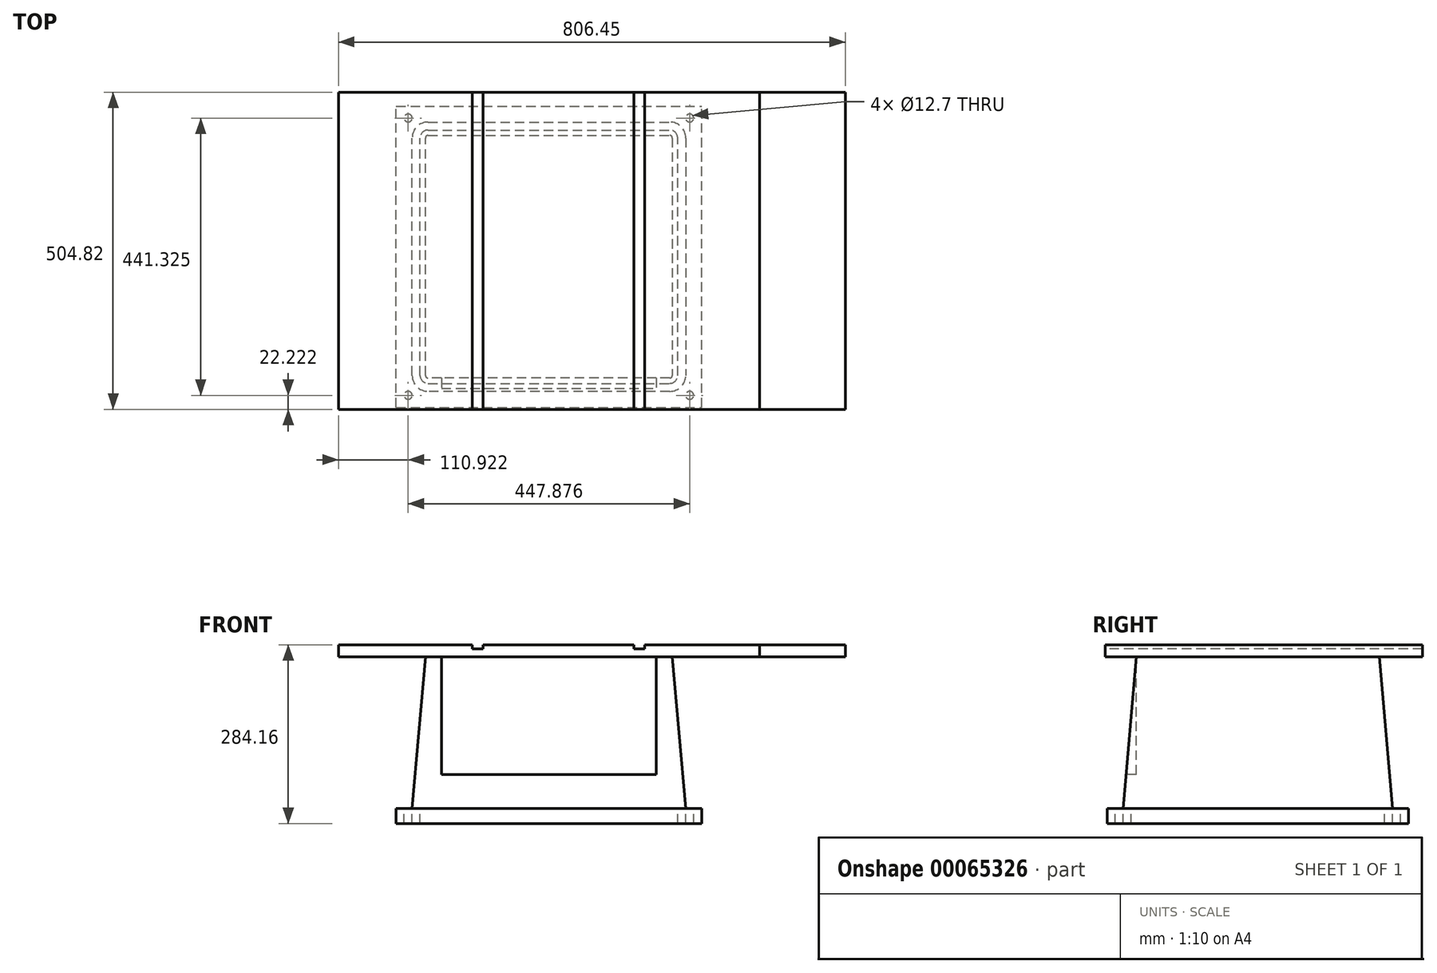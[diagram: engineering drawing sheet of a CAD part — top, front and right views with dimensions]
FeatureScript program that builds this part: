
annotation { "Feature Type Name" : "Feature", "Feature Type Description" : "" }
export const myFeature = defineFeature(function(context is Context, id is Id, definition is map)
    precondition{}
    {
        {
            var Q0;
            Q0=qCreatedBy(makeId("Top.planeOp"),FACE);
            var sketch = newSketch(context, id + "F0", { "sketchPlane" : qUnion([Q0])});
            skLineSegment(sketch, "E0.bottom", {"start": v(334.96, 252.41) * mm, "end": v(-334.96, 252.41) * mm});
            skLineSegment(sketch, "E0.top", {"start": v(334.96, -252.41) * mm, "end": v(-334.96, -252.41) * mm});
            skLineSegment(sketch, "E0.left", {"start": v(334.96, 252.41) * mm, "end": v(334.96, -252.41) * mm});
            skLineSegment(sketch, "E0.right", {"start": v(-334.96, 252.41) * mm, "end": v(-334.96, -252.41) * mm});
            skPoint(sketch, "E0.middle", {"position": v(0, 0) * mm});
            skSolve(sketch);
        }
        {
            var Q0;
            Q0=makeQuery(id+"F0.imprint","IMPRINT",FACE,{"disambiguationData":[TD([[makeQuery(id+"F0.imprint","IMPRINT",EDGE,{"derivedFrom":sQuery(id+"F0.wireOp",EDGE,"E0.bottom")}),1.0]])]});
            extrude(context, id + "F1", {"entities" : qUnion([Q0]), "oppositeDirection" : true, "depth" : 19.05 * mm, "offsetDistance" : 25.4 * mm});
        }
        {
            var Q0;
            Q0=makeQuery(id+"F1.opExtrude","SWEPT_FACE",FACE,{"disambiguationData":[OSD([sQuery(id+"F0.wireOp",EDGE,"E0.left")])]});
            extrude(context, id + "F2", {"entities" : qUnion([Q0]), "depth" : 136.53 * mm, "offsetDistance" : 25.4 * mm});
        }
        {
            var Q0;
            Q0=makeQuery(id+"F0.imprint","IMPRINT",FACE,{"disambiguationData":[TD([[makeQuery(id+"F0.imprint","IMPRINT",EDGE,{"derivedFrom":sQuery(id+"F0.wireOp",EDGE,"E0.bottom")}),1.0]])]});
            cPlane(context, id + "F3", {"entities" : qUnion([Q0]), "cplaneType" : CPlaneType.OFFSET, "offset" : 260.35 * mm, "oppositeDirection" : true, "width" : 152.4 * mm, "height" : 152.4 * mm});
        }
        {
            var Q0;
            Q0=qCreatedBy(id+"F3.planeOp",FACE);
            var sketch = newSketch(context, id + "F4", { "sketchPlane" : qUnion([Q0])});
            skLineSegment(sketch, "E1.bottom", {"start": v(-243.09, -249.24) * mm, "end": v(242.89, -249.24) * mm});
            skLineSegment(sketch, "E1.top", {"start": v(-243.09, 230.19) * mm, "end": v(242.89, 230.19) * mm});
            skLineSegment(sketch, "E1.left", {"start": v(-243.09, -249.24) * mm, "end": v(-243.09, 230.19) * mm});
            skLineSegment(sketch, "E1.right", {"start": v(242.89, -249.24) * mm, "end": v(242.89, 230.19) * mm});
            skLineSegment(sketch, "E2.bottom", {"start": v(-224.04, 211.14) * mm, "end": v(223.84, 211.14) * mm, "construction": true});
            skLineSegment(sketch, "E2.top", {"start": v(-224.04, -230.19) * mm, "end": v(223.84, -230.19) * mm, "construction": true});
            skLineSegment(sketch, "E2.left", {"start": v(-224.04, 211.14) * mm, "end": v(-224.04, -230.19) * mm, "construction": true});
            skLineSegment(sketch, "E2.right", {"start": v(223.84, 211.14) * mm, "end": v(223.84, -230.19) * mm, "construction": true});
            skCircle(sketch, "E3", {"center": v(-224.04, 211.14) * mm, "radius": 6.35 * mm});
            skCircle(sketch, "E4", {"center": v(-224.04, -230.19) * mm, "radius": 6.35 * mm});
            skCircle(sketch, "E5", {"center": v(223.84, -230.19) * mm, "radius": 6.35 * mm});
            skCircle(sketch, "E6", {"center": v(223.84, 211.14) * mm, "radius": 6.35 * mm});
            skLineSegment(sketch, "E7.bottom", {"start": v(-192.29, -223.84) * mm, "end": v(192.09, -223.84) * mm});
            skLineSegment(sketch, "E7.top", {"start": v(-192.29, 204.79) * mm, "end": v(192.09, 204.79) * mm});
            skLineSegment(sketch, "E7.left", {"start": v(-217.69, -198.44) * mm, "end": v(-217.69, 179.39) * mm});
            skLineSegment(sketch, "E7.right", {"start": v(217.49, -198.44) * mm, "end": v(217.49, 179.39) * mm});
            skPoint(sketch, "E8.visualSharp", {"position": v(217.49, 204.79) * mm});
            skArc(sketch, "E8.filletArc", {"start": v(217.49, 179.39) * mm, "mid": v(210.05, 197.35) * mm, "end": v(192.09, 204.79) * mm});
            skPoint(sketch, "E9.visualSharp", {"position": v(-217.69, 204.79) * mm});
            skArc(sketch, "E9.filletArc", {"start": v(-192.29, 204.79) * mm, "mid": v(-210.25, 197.35) * mm, "end": v(-217.69, 179.39) * mm});
            skPoint(sketch, "E10.visualSharp", {"position": v(-217.69, -223.84) * mm});
            skArc(sketch, "E10.filletArc", {"start": v(-217.69, -198.44) * mm, "mid": v(-210.25, -216.4) * mm, "end": v(-192.29, -223.84) * mm});
            skPoint(sketch, "E11.visualSharp", {"position": v(217.49, -223.84) * mm});
            skArc(sketch, "E11.filletArc", {"start": v(192.09, -223.84) * mm, "mid": v(210.05, -216.4) * mm, "end": v(217.49, -198.44) * mm});
            skSolve(sketch);
        }
        {
            var Q0;
            Q0=makeQuery(id+"F4.imprint","IMPRINT",FACE,{"disambiguationData":[TD([[makeQuery(id+"F4.imprint","IMPRINT",EDGE,{"derivedFrom":sQuery(id+"F4.wireOp",EDGE,"E7.bottom")}),1.0]])]});
            extrude(context, id + "F5", {"entities" : qUnion([Q0]), "operationType" : NewBodyOperationType.ADD, "endBound" : BoundingType.UP_TO_NEXT, "depth" : 25.4 * mm, "offsetDistance" : 25.4 * mm, "hasDraft" : true, "draftAngle" : 5 * degree, "draftPullDirection" : true});
        }
        {
            var Q0;
            Q0=makeQuery(id+"F5.opExtrude","CAP_FACE",FACE,{"disambiguationData":[OSD([sQuery(id+"F4.wireOp",EDGE,"E7.bottom"),sQuery(id+"F4.wireOp",EDGE,"E7.top"),sQuery(id+"F4.wireOp",EDGE,"E7.left"),sQuery(id+"F4.wireOp",EDGE,"E7.right"),sQuery(id+"F4.wireOp",EDGE,"E8.filletArc"),sQuery(id+"F4.wireOp",EDGE,"E9.filletArc"),sQuery(id+"F4.wireOp",EDGE,"E10.filletArc"),sQuery(id+"F4.wireOp",EDGE,"E11.filletArc")])],"isStart":true});
            var sketch = newSketch(context, id + "F6", { "sketchPlane" : qUnion([Q0])});
            skLineSegment(sketch, "E12.0", {"start": v(-192.29, 223.84) * mm, "end": v(192.09, 223.84) * mm});
            skLineSegment(sketch, "E13.0.0", {"start": v(-192.29, -204.79) * mm, "end": v(192.09, -204.79) * mm});
            skArc(sketch, "E13.0.1", {"start": v(192.09, -204.79) * mm, "mid": v(210.05, -197.35) * mm, "end": v(217.49, -179.39) * mm});
            skLineSegment(sketch, "E13.0.2", {"start": v(217.49, 198.44) * mm, "end": v(217.49, -179.39) * mm});
            skArc(sketch, "E13.0.3", {"start": v(217.49, 198.44) * mm, "mid": v(210.05, 216.4) * mm, "end": v(192.09, 223.84) * mm});
            skArc(sketch, "E13.0.5", {"start": v(-192.29, 223.84) * mm, "mid": v(-210.25, 216.4) * mm, "end": v(-217.69, 198.44) * mm});
            skLineSegment(sketch, "E13.0.6", {"start": v(-217.69, 198.44) * mm, "end": v(-217.69, -179.39) * mm});
            skArc(sketch, "E13.0.7", {"start": v(-217.69, -179.39) * mm, "mid": v(-210.25, -197.35) * mm, "end": v(-192.29, -204.79) * mm});
            skArc(sketch, "E14.0", {"start": v(-204.99, -179.39) * mm, "mid": v(-201.27, -188.37) * mm, "end": v(-192.29, -192.09) * mm});
            skLineSegment(sketch, "E14.1", {"start": v(-204.99, 198.44) * mm, "end": v(-204.99, -179.39) * mm});
            skLineSegment(sketch, "E14.2", {"start": v(-192.29, -192.09) * mm, "end": v(192.09, -192.09) * mm});
            skArc(sketch, "E14.3", {"start": v(-192.29, 211.14) * mm, "mid": v(-201.27, 207.42) * mm, "end": v(-204.99, 198.44) * mm});
            skArc(sketch, "E14.4", {"start": v(192.09, -192.09) * mm, "mid": v(201.07, -188.37) * mm, "end": v(204.79, -179.39) * mm});
            skLineSegment(sketch, "E14.5", {"start": v(204.79, 198.44) * mm, "end": v(204.79, -179.39) * mm});
            skArc(sketch, "E14.6", {"start": v(204.79, 198.44) * mm, "mid": v(201.07, 207.42) * mm, "end": v(192.09, 211.14) * mm});
            skLineSegment(sketch, "E14.7", {"start": v(-192.29, 211.14) * mm, "end": v(192.09, 211.14) * mm});
            skSolve(sketch);
        }
        {
            var Q0;
            Q0=makeQuery(id+"F6.imprint","IMPRINT",FACE,{"disambiguationData":[TD([[makeQuery(id+"F6.imprint","IMPRINT",EDGE,{"derivedFrom":sQuery(id+"F6.wireOp",EDGE,"E13.0.0")}),1.0]])]});
            extrude(context, id + "F7", {"entities" : qUnion([Q0]), "operationType" : NewBodyOperationType.ADD, "depth" : 23.8 * mm, "offsetDistance" : 25.4 * mm});
        }
        {
            var Q0;
            Q0 = qSketchRegion(id + "F4", true);
            extrude(context, id + "F8", {"entities" : qUnion([Q0]), "operationType" : NewBodyOperationType.ADD, "oppositeDirection" : true, "depth" : 23.8 * mm, "offsetDistance" : 25.4 * mm});
        }
        {
            var Q0;
            Q0=makeQuery(id+"F1.opExtrude","CAP_FACE",FACE,{"disambiguationData":[OSD([sQuery(id+"F0.wireOp",EDGE,"E0.bottom"),sQuery(id+"F0.wireOp",EDGE,"E0.top"),sQuery(id+"F0.wireOp",EDGE,"E0.left"),sQuery(id+"F0.wireOp",EDGE,"E0.right")])],"isStart":false});
            var sketch = newSketch(context, id + "F9", { "sketchPlane" : qUnion([Q0])});
            skLineSegment(sketch, "E15.bottom", {"start": v(-171.18, 202.73) * mm, "end": v(170.98, 202.73) * mm});
            skLineSegment(sketch, "E15.top", {"start": v(-171.18, 252.41) * mm, "end": v(170.98, 252.41) * mm});
            skLineSegment(sketch, "E15.left", {"start": v(-171.18, 202.73) * mm, "end": v(-171.18, 252.41) * mm});
            skLineSegment(sketch, "E15.right", {"start": v(170.98, 202.73) * mm, "end": v(170.98, 252.41) * mm});
            skSolve(sketch);
        }
        {
            var Q0;
            Q0 = qSketchRegion(id + "F9", true);
            extrude(context, id + "F10", {"entities" : qUnion([Q0]), "operationType" : NewBodyOperationType.REMOVE, "depth" : 186.94 * mm, "offsetDistance" : 25.4 * mm});
        }
        {
            var Q0;
            Q0=makeQuery(id+"F1.opExtrude","SWEPT_FACE",FACE,{"disambiguationData":[OSD([sQuery(id+"F0.wireOp",EDGE,"E0.top")])]});
            var sketch = newSketch(context, id + "F11", { "sketchPlane" : qUnion([Q0])});
            skLineSegment(sketch, "E16.bottom", {"start": v(-122.24, 0) * mm, "end": v(-104.78, 0) * mm});
            skLineSegment(sketch, "E16.top", {"start": v(-122.24, -6.35) * mm, "end": v(-104.78, -6.35) * mm});
            skLineSegment(sketch, "E16.left", {"start": v(-122.24, 0) * mm, "end": v(-122.24, -6.35) * mm});
            skLineSegment(sketch, "E16.right", {"start": v(-104.78, 0) * mm, "end": v(-104.78, -6.35) * mm});
            skLineSegment(sketch, "E17.bottom", {"start": v(134.94, 0) * mm, "end": v(152.4, 0) * mm});
            skLineSegment(sketch, "E17.top", {"start": v(134.94, -6.35) * mm, "end": v(152.4, -6.35) * mm});
            skLineSegment(sketch, "E17.left", {"start": v(134.94, 0) * mm, "end": v(134.94, -6.35) * mm});
            skLineSegment(sketch, "E17.right", {"start": v(152.4, 0) * mm, "end": v(152.4, -6.35) * mm});
            skSolve(sketch);
        }
        {
            var Q0;
            Q0 = qSketchRegion(id + "F11", true);
            extrude(context, id + "F12", {"entities" : qUnion([Q0]), "operationType" : NewBodyOperationType.REMOVE, "endBound" : BoundingType.UP_TO_NEXT, "oppositeDirection" : true, "depth" : 25.4 * mm, "offsetDistance" : 25.4 * mm});
        }
    });
